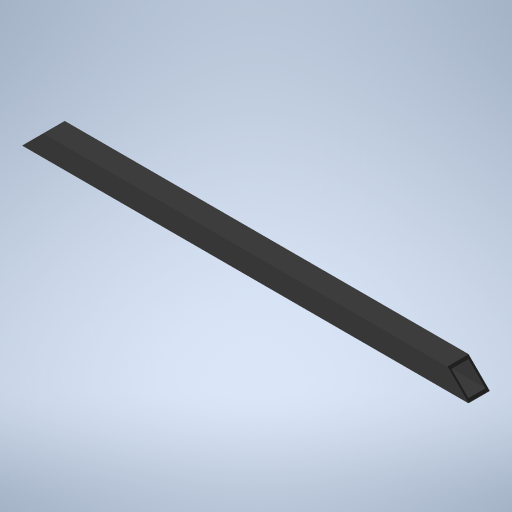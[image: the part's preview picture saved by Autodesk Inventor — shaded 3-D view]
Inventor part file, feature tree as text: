
AUTODESK INVENTOR PART (.ipt)
format: ipt  version: 2024.3 (Build 283343000, 343)  size: 251,904 bytes
history: native  units: mm
features: extrude x2, sketch x2
ambient origin geometry x8: Origin, YZ Plane, XZ Plane, XY Plane, X Axis, Y Axis, Z Axis, Center Point
bodies: Solid1 (feature_tree)
feature tree (4):
  extrude  "Extrusion1"  Depth=2.0mm
  extrude  "Extrusion2"  Depth=19.0mm
  sketch  "Sketch1"  dims[d0=2.0mm d1=2.0mm]
  sketch  "Sketch2"  dims[d2=19.0mm d3=19.0mm d4=400.0mm d5=0.0mm d8=10.0mm d9=0.0mm d10=45.0deg d11=45.0deg]
